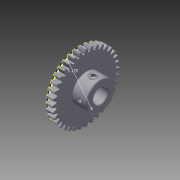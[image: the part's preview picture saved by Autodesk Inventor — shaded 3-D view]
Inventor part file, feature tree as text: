
AUTODESK INVENTOR PART (.ipt)
format: ipt  version: 2012 (Build 160160000, 160)  size: 912,896 bytes
history: native  units: in
note: dims shown in document units (in); Inventor stores cm internally (conversion verified against a paired STEP export)
features: imported_body x2, sketch x1
ambient origin geometry x8: Origin, YZ Plane, XZ Plane, XY Plane, X Axis, Y Axis, Z Axis, Center Point
feature tree (3):
  sketch  "Sketch1"  dims[d0=1.125in]
  imported_body  "Base1"
  imported_body  "Base2"
